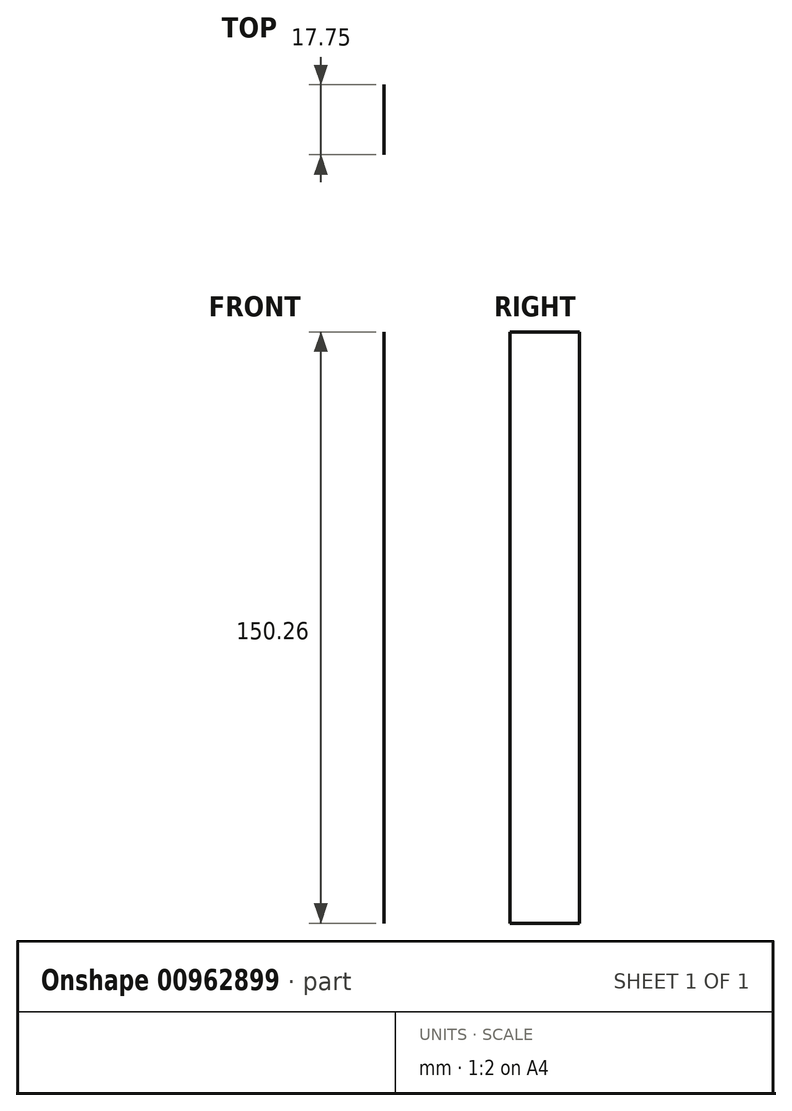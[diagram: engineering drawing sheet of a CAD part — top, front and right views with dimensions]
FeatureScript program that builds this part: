
annotation { "Feature Type Name" : "Feature", "Feature Type Description" : "" }
export const myFeature = defineFeature(function(context is Context, id is Id, definition is map)
    precondition{}
    {
        {
            var Q0;
            Q0=qCreatedBy(makeId("Front.planeOp"),FACE);
            var sketch = newSketch(context, id + "F0", { "sketchPlane" : qUnion([Q0])});
            skLineSegment(sketch, "E0.bottom", {"start": v(73.9, -74.53) * mm, "end": v(53.32, -74.53) * mm});
            skLineSegment(sketch, "E0.top", {"start": v(73.9, 75.73) * mm, "end": v(53.32, 75.73) * mm});
            skLineSegment(sketch, "E0.left", {"start": v(73.9, -74.53) * mm, "end": v(73.9, 75.73) * mm});
            skLineSegment(sketch, "E0.right", {"start": v(53.32, -74.53) * mm, "end": v(53.32, 75.73) * mm});
            skSolve(sketch);
        }
        {
            var Q0;
            Q0=sQuery(id+"F0.wireOp",EDGE,"E0.left");
            extrude(context, id + "F1", {"bodyType" : ToolBodyType.SURFACE, "surfaceEntities" : qUnion([Q0]), "depth" : 17.75 * mm, "offsetDistance" : 25 * mm});
        }
    });
